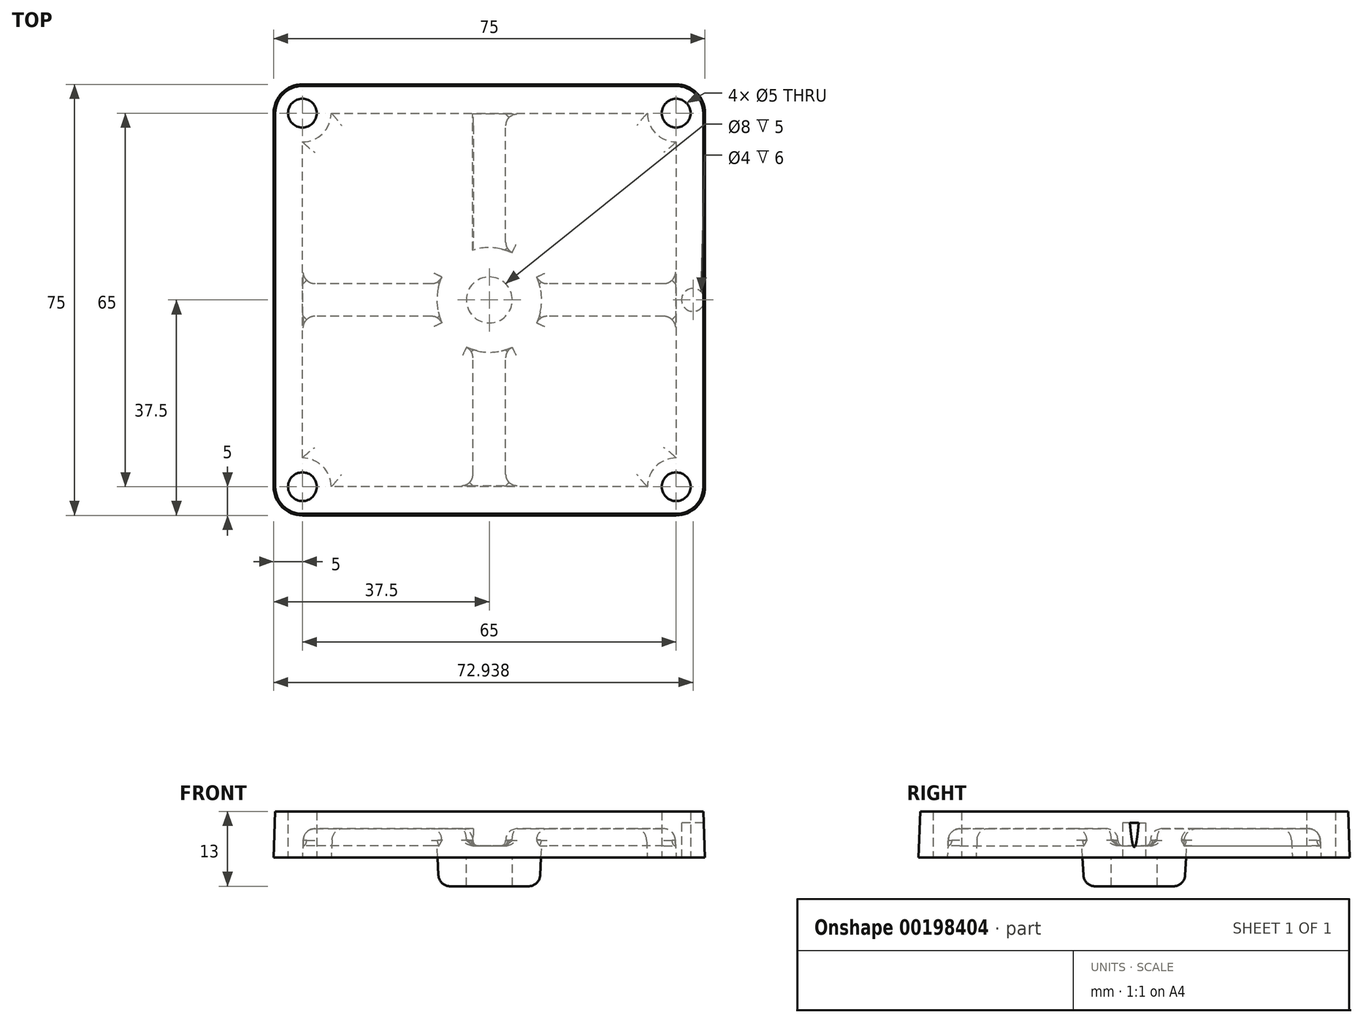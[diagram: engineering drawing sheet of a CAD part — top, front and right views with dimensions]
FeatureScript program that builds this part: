
annotation { "Feature Type Name" : "Feature", "Feature Type Description" : "" }
export const myFeature = defineFeature(function(context is Context, id is Id, definition is map)
    precondition{}
    {
        {
            var Q0;
            Q0=qCreatedBy(makeId("Top.planeOp"),FACE);
            var sketch = newSketch(context, id + "F0", { "sketchPlane" : qUnion([Q0])});
            skLineSegment(sketch, "E0.bottom", {"start": v(-32.5, -37.5) * mm, "end": v(32.5, -37.5) * mm});
            skLineSegment(sketch, "E0.top", {"start": v(-32.5, 37.5) * mm, "end": v(32.5, 37.5) * mm});
            skLineSegment(sketch, "E0.left", {"start": v(-37.5, -32.5) * mm, "end": v(-37.5, 32.5) * mm});
            skLineSegment(sketch, "E0.right", {"start": v(37.5, -32.5) * mm, "end": v(37.5, 32.5) * mm});
            skPoint(sketch, "E0.middle", {"position": v(0, 0) * mm});
            skPoint(sketch, "E1.visualSharp", {"position": v(-37.5, 37.5) * mm});
            skArc(sketch, "E1.filletArc", {"start": v(-32.5, 37.5) * mm, "mid": v(-36.04, 36.04) * mm, "end": v(-37.5, 32.5) * mm});
            skPoint(sketch, "E2.visualSharp", {"position": v(37.5, 37.5) * mm});
            skArc(sketch, "E2.filletArc", {"start": v(37.5, 32.5) * mm, "mid": v(36.04, 36.04) * mm, "end": v(32.5, 37.5) * mm});
            skPoint(sketch, "E3.visualSharp", {"position": v(37.5, -37.5) * mm});
            skArc(sketch, "E3.filletArc", {"start": v(32.5, -37.5) * mm, "mid": v(36.04, -36.04) * mm, "end": v(37.5, -32.5) * mm});
            skPoint(sketch, "E4.visualSharp", {"position": v(-37.5, -37.5) * mm});
            skArc(sketch, "E4.filletArc", {"start": v(-37.5, -32.5) * mm, "mid": v(-36.04, -36.04) * mm, "end": v(-32.5, -37.5) * mm});
            skSolve(sketch);
        }
        {
            var Q0;
            Q0=makeQuery(id+"F0.imprint","IMPRINT",FACE,{"disambiguationData":[TD([[makeQuery(id+"F0.imprint","IMPRINT",EDGE,{"derivedFrom":sQuery(id+"F0.wireOp",EDGE,"E0.bottom")}),1.0]])]});
            extrude(context, id + "F1", {"entities" : qUnion([Q0]), "depth" : 8 * mm, "hasDraft" : true, "draftAngle" : 2 * degree, "draftPullDirection" : true, "offsetDistance" : 25 * mm});
        }
        {
            var Q0;
            Q0=qCreatedBy(makeId("Top.planeOp"),FACE);
            var sketch = newSketch(context, id + "F2", { "sketchPlane" : qUnion([Q0])});
            skCircle(sketch, "E5", {"center": v(0, 0) * mm, "radius": 9 * mm});
            skLineSegment(sketch, "E6.bottom", {"start": v(-27.5, -32.5) * mm, "end": v(27.5, -32.5) * mm});
            skLineSegment(sketch, "E6.top", {"start": v(-27.5, 32.5) * mm, "end": v(27.5, 32.5) * mm});
            skLineSegment(sketch, "E6.left", {"start": v(-32.5, -27.5) * mm, "end": v(-32.5, 27.5) * mm});
            skLineSegment(sketch, "E6.right", {"start": v(32.5, -27.5) * mm, "end": v(32.5, 27.5) * mm});
            skArc(sketch, "E7", {"start": v(-27.5, 32.5) * mm, "mid": v(-28.96, 28.96) * mm, "end": v(-32.5, 27.5) * mm});
            skArc(sketch, "E8", {"start": v(-32.5, -27.5) * mm, "mid": v(-28.96, -28.96) * mm, "end": v(-27.5, -32.5) * mm});
            skArc(sketch, "E9", {"start": v(27.5, -32.5) * mm, "mid": v(28.96, -28.96) * mm, "end": v(32.5, -27.5) * mm});
            skArc(sketch, "E10", {"start": v(27.5, 32.5) * mm, "mid": v(28.96, 28.96) * mm, "end": v(32.5, 27.5) * mm});
            skSolve(sketch);
        }
        {
            var Q0;
            Q0=makeQuery(id+"F2.imprint","IMPRINT",FACE,{"disambiguationData":[TD([[makeQuery(id+"F2.imprint","IMPRINT",EDGE,{"derivedFrom":sQuery(id+"F2.wireOp",EDGE,"E5")}),-1.0]])]});
            extrude(context, id + "F3", {"entities" : qUnion([Q0]), "operationType" : NewBodyOperationType.REMOVE, "depth" : 5 * mm, "hasDraft" : true, "draftAngle" : 3 * degree, "draftPullDirection" : true, "offsetDistance" : 25 * mm});
        }
        {
            var Q0;
            Q0=makeQuery(id+"F3.boolean.opBoolean","COPY",EDGE,{"derivedFrom":makeQuery(id+"F3.opExtrude","CAP_EDGE",EDGE,{"disambiguationData":[OSD([sQuery(id+"F2.wireOp",EDGE,"E6.top")])],"isStart":false})});
            var Q1;
            Q1=makeQuery(id+"F3.boolean.opBoolean","COPY",EDGE,{"derivedFrom":makeQuery(id+"F3.opExtrude","CAP_EDGE",EDGE,{"disambiguationData":[OSD([sQuery(id+"F2.wireOp",EDGE,"E7")])],"isStart":false})});
            var Q2;
            Q2=makeQuery(id+"F3.boolean.opBoolean","COPY",EDGE,{"derivedFrom":makeQuery(id+"F3.opExtrude","CAP_EDGE",EDGE,{"disambiguationData":[OSD([sQuery(id+"F2.wireOp",EDGE,"E10")])],"isStart":false})});
            var Q3;
            Q3=makeQuery(id+"F3.boolean.opBoolean","COPY",EDGE,{"derivedFrom":makeQuery(id+"F3.opExtrude","CAP_EDGE",EDGE,{"disambiguationData":[OSD([sQuery(id+"F2.wireOp",EDGE,"E6.right")])],"isStart":false})});
            var Q4;
            Q4=makeQuery(id+"F3.boolean.opBoolean","COPY",EDGE,{"derivedFrom":makeQuery(id+"F3.opExtrude","CAP_EDGE",EDGE,{"disambiguationData":[OSD([sQuery(id+"F2.wireOp",EDGE,"E9")])],"isStart":false})});
            var Q5;
            Q5=makeQuery(id+"F3.boolean.opBoolean","COPY",EDGE,{"derivedFrom":makeQuery(id+"F3.opExtrude","CAP_EDGE",EDGE,{"disambiguationData":[OSD([sQuery(id+"F2.wireOp",EDGE,"E8")])],"isStart":false})});
            var Q6;
            Q6=makeQuery(id+"F3.boolean.opBoolean","COPY",EDGE,{"derivedFrom":makeQuery(id+"F3.opExtrude","CAP_EDGE",EDGE,{"disambiguationData":[OSD([sQuery(id+"F2.wireOp",EDGE,"E6.bottom")])],"isStart":false})});
            var Q7;
            Q7=makeQuery(id+"F3.boolean.opBoolean","COPY",EDGE,{"derivedFrom":makeQuery(id+"F3.opExtrude","CAP_EDGE",EDGE,{"disambiguationData":[OSD([sQuery(id+"F2.wireOp",EDGE,"E6.left")])],"isStart":false})});
            fillet(context, id + "F4", {"entities" : qUnion([Q0, Q1, Q2, Q3, Q4, Q5, Q6, Q7]), "radius" : 2 * mm, "tangentPropagation" : true, "allowEdgeOverflow" : false});
        }
        {
            var Q0;
            Q0=qCreatedBy(makeId("Top.planeOp"),FACE);
            var sketch = newSketch(context, id + "F5", { "sketchPlane" : qUnion([Q0])});
            skPoint(sketch, "E11.middle", {"position": v(0, 0) * mm});
            skCircle(sketch, "E12", {"center": v(-32.5, 32.5) * mm, "radius": 2.5 * mm});
            skPoint(sketch, "E11.right.start.orphan", {"position": v(32.5, 32.5) * mm});
            skPoint(sketch, "E11.top.end.orphan", {"position": v(32.5, -32.5) * mm});
            skPoint(sketch, "E11.top.start.orphan", {"position": v(-32.5, -32.5) * mm});
            skCircle(sketch, "E13", {"center": v(-32.5, -32.5) * mm, "radius": 2.5 * mm});
            skCircle(sketch, "E14", {"center": v(32.5, -32.5) * mm, "radius": 2.5 * mm});
            skCircle(sketch, "E15", {"center": v(32.5, 32.5) * mm, "radius": 2.5 * mm});
            skSolve(sketch);
        }
        {
            var Q0;
            Q0=makeQuery(id+"F5.imprint","IMPRINT",FACE,{"disambiguationData":[TD([[makeQuery(id+"F5.imprint","IMPRINT",EDGE,{"derivedFrom":sQuery(id+"F5.wireOp",EDGE,"E13")}),1.0]])]});
            var Q1;
            Q1=makeQuery(id+"F5.imprint","IMPRINT",FACE,{"disambiguationData":[TD([[makeQuery(id+"F5.imprint","IMPRINT",EDGE,{"derivedFrom":sQuery(id+"F5.wireOp",EDGE,"E12")}),1.0]])]});
            var Q2;
            Q2=makeQuery(id+"F5.imprint","IMPRINT",FACE,{"disambiguationData":[TD([[makeQuery(id+"F5.imprint","IMPRINT",EDGE,{"derivedFrom":sQuery(id+"F5.wireOp",EDGE,"E15")}),1.0]])]});
            var Q3;
            Q3=makeQuery(id+"F5.imprint","IMPRINT",FACE,{"disambiguationData":[TD([[makeQuery(id+"F5.imprint","IMPRINT",EDGE,{"derivedFrom":sQuery(id+"F5.wireOp",EDGE,"E14")}),1.0]])]});
            extrude(context, id + "F6", {"entities" : qUnion([Q0, Q1, Q2, Q3]), "operationType" : NewBodyOperationType.REMOVE, "depth" : 25 * mm, "hasSecondDirection" : true, "secondDirectionOppositeDirection" : true, "secondDirectionDepth" : 25 * mm});
        }
        {
            var Q0;
            Q0=makeQuery(id+"F3.boolean.opBoolean","COPY",EDGE,{"derivedFrom":makeQuery(id+"F3.opExtrude","CAP_EDGE",EDGE,{"disambiguationData":[OSD([sQuery(id+"F2.wireOp",EDGE,"E5")])],"isStart":false})});
            fillet(context, id + "F7", {"entities" : qUnion([Q0]), "radius" : 2 * mm, "tangentPropagation" : true, "allowEdgeOverflow" : false});
        }
        {
            var Q0;
            Q0=qCreatedBy(makeId("Top.planeOp"),FACE);
            var sketch = newSketch(context, id + "F8", { "sketchPlane" : qUnion([Q0])});
            skLineSegment(sketch, "E16.bottom", {"start": v(-35, -3) * mm, "end": v(-3, -3) * mm});
            skLineSegment(sketch, "E16.top", {"start": v(-35, 3) * mm, "end": v(-3, 3) * mm});
            skLineSegment(sketch, "E16.left", {"start": v(-35, -3) * mm, "end": v(-35, 3) * mm});
            skLineSegment(sketch, "E16.right", {"start": v(35, -3) * mm, "end": v(35, 3) * mm});
            skPoint(sketch, "E16.middle", {"position": v(0, 0) * mm});
            skLineSegment(sketch, "E17.bottom", {"start": v(3, 35) * mm, "end": v(-3, 35) * mm});
            skLineSegment(sketch, "E17.top", {"start": v(3, -35) * mm, "end": v(-3, -35) * mm});
            skLineSegment(sketch, "E17.left", {"start": v(3, 35) * mm, "end": v(3, 3) * mm});
            skLineSegment(sketch, "E17.right", {"start": v(-3, 35) * mm, "end": v(-3, 3) * mm});
            skLineSegment(sketch, "E18.trimOffspring", {"start": v(-3, -3) * mm, "end": v(-3, -35) * mm});
            skLineSegment(sketch, "E19.trimOffspring", {"start": v(3, -3) * mm, "end": v(35, -3) * mm});
            skLineSegment(sketch, "E20.trimOffspring", {"start": v(3, -3) * mm, "end": v(3, -35) * mm});
            skLineSegment(sketch, "E21.trimOffspring", {"start": v(3, 3) * mm, "end": v(35, 3) * mm});
            skSolve(sketch);
        }
        {
            var Q0;
            Q0 = qSketchRegion(id + "F8", true);
            extrude(context, id + "F9", {"entities" : qUnion([Q0]), "operationType" : NewBodyOperationType.ADD, "depth" : 7 * mm, "hasDraft" : true, "draftAngle" : 3 * degree, "draftPullDirection" : true, "hasSecondDirection" : true, "secondDirectionOppositeDirection" : false, "secondDirectionDepth" : 2 * mm, "offsetDistance" : 25 * mm});
        }
        {
            var Q0;
            Q0=makeQuery(id+"F9.boolean.opBoolean","INTERSECT",EDGE,{"derivedFrom":[makeQuery(id+"F3.boolean.opBoolean","COPY",FACE,{"derivedFrom":makeQuery(id+"F3.opExtrude","CAP_FACE",FACE,{"disambiguationData":[OSD([sQuery(id+"F2.wireOp",EDGE,"E5"),sQuery(id+"F2.wireOp",EDGE,"E6.bottom"),sQuery(id+"F2.wireOp",EDGE,"E6.top"),sQuery(id+"F2.wireOp",EDGE,"E6.left"),sQuery(id+"F2.wireOp",EDGE,"E6.right"),sQuery(id+"F2.wireOp",EDGE,"E7"),sQuery(id+"F2.wireOp",EDGE,"E8"),sQuery(id+"F2.wireOp",EDGE,"E9"),sQuery(id+"F2.wireOp",EDGE,"E10")])],"isStart":false})}),makeQuery(id+"F9.opExtrude","SWEPT_FACE",FACE,{"disambiguationData":[OSD([sQuery(id+"F8.wireOp",EDGE,"E18.trimOffspring")])]})]});
            var Q1;
            Q1=makeQuery(id+"F9.boolean.opBoolean","INTERSECT",EDGE,{"derivedFrom":[makeQuery(id+"F3.boolean.opBoolean","COPY",FACE,{"derivedFrom":makeQuery(id+"F3.opExtrude","CAP_FACE",FACE,{"disambiguationData":[OSD([sQuery(id+"F2.wireOp",EDGE,"E5"),sQuery(id+"F2.wireOp",EDGE,"E6.bottom"),sQuery(id+"F2.wireOp",EDGE,"E6.top"),sQuery(id+"F2.wireOp",EDGE,"E6.left"),sQuery(id+"F2.wireOp",EDGE,"E6.right"),sQuery(id+"F2.wireOp",EDGE,"E7"),sQuery(id+"F2.wireOp",EDGE,"E8"),sQuery(id+"F2.wireOp",EDGE,"E9"),sQuery(id+"F2.wireOp",EDGE,"E10")])],"isStart":false})}),makeQuery(id+"F9.opExtrude","SWEPT_FACE",FACE,{"disambiguationData":[OSD([sQuery(id+"F8.wireOp",EDGE,"E16.bottom")])]})]});
            var Q2;
            Q2=makeQuery(id+"F9.boolean.opBoolean","INTERSECT",EDGE,{"derivedFrom":[makeQuery(id+"F3.boolean.opBoolean","COPY",FACE,{"derivedFrom":makeQuery(id+"F3.opExtrude","CAP_FACE",FACE,{"disambiguationData":[OSD([sQuery(id+"F2.wireOp",EDGE,"E5"),sQuery(id+"F2.wireOp",EDGE,"E6.bottom"),sQuery(id+"F2.wireOp",EDGE,"E6.top"),sQuery(id+"F2.wireOp",EDGE,"E6.left"),sQuery(id+"F2.wireOp",EDGE,"E6.right"),sQuery(id+"F2.wireOp",EDGE,"E7"),sQuery(id+"F2.wireOp",EDGE,"E8"),sQuery(id+"F2.wireOp",EDGE,"E9"),sQuery(id+"F2.wireOp",EDGE,"E10")])],"isStart":false})}),makeQuery(id+"F9.opExtrude","SWEPT_FACE",FACE,{"disambiguationData":[OSD([sQuery(id+"F8.wireOp",EDGE,"E19.trimOffspring")])]})]});
            var Q3;
            Q3=makeQuery(id+"F9.boolean.opBoolean","INTERSECT",EDGE,{"derivedFrom":[makeQuery(id+"F3.boolean.opBoolean","COPY",FACE,{"derivedFrom":makeQuery(id+"F3.opExtrude","CAP_FACE",FACE,{"disambiguationData":[OSD([sQuery(id+"F2.wireOp",EDGE,"E5"),sQuery(id+"F2.wireOp",EDGE,"E6.bottom"),sQuery(id+"F2.wireOp",EDGE,"E6.top"),sQuery(id+"F2.wireOp",EDGE,"E6.left"),sQuery(id+"F2.wireOp",EDGE,"E6.right"),sQuery(id+"F2.wireOp",EDGE,"E7"),sQuery(id+"F2.wireOp",EDGE,"E8"),sQuery(id+"F2.wireOp",EDGE,"E9"),sQuery(id+"F2.wireOp",EDGE,"E10")])],"isStart":false})}),makeQuery(id+"F9.opExtrude","SWEPT_FACE",FACE,{"disambiguationData":[OSD([sQuery(id+"F8.wireOp",EDGE,"E21.trimOffspring")])]})]});
            var Q4;
            Q4=makeQuery(id+"F9.boolean.opBoolean","INTERSECT",EDGE,{"derivedFrom":[makeQuery(id+"F3.boolean.opBoolean","COPY",FACE,{"derivedFrom":makeQuery(id+"F3.opExtrude","CAP_FACE",FACE,{"disambiguationData":[OSD([sQuery(id+"F2.wireOp",EDGE,"E5"),sQuery(id+"F2.wireOp",EDGE,"E6.bottom"),sQuery(id+"F2.wireOp",EDGE,"E6.top"),sQuery(id+"F2.wireOp",EDGE,"E6.left"),sQuery(id+"F2.wireOp",EDGE,"E6.right"),sQuery(id+"F2.wireOp",EDGE,"E7"),sQuery(id+"F2.wireOp",EDGE,"E8"),sQuery(id+"F2.wireOp",EDGE,"E9"),sQuery(id+"F2.wireOp",EDGE,"E10")])],"isStart":false})}),makeQuery(id+"F9.opExtrude","SWEPT_FACE",FACE,{"disambiguationData":[OSD([sQuery(id+"F8.wireOp",EDGE,"E16.top")])]})]});
            var Q5;
            Q5=makeQuery(id+"F9.boolean.opBoolean","INTERSECT",EDGE,{"derivedFrom":[makeQuery(id+"F3.boolean.opBoolean","COPY",FACE,{"derivedFrom":makeQuery(id+"F3.opExtrude","CAP_FACE",FACE,{"disambiguationData":[OSD([sQuery(id+"F2.wireOp",EDGE,"E5"),sQuery(id+"F2.wireOp",EDGE,"E6.bottom"),sQuery(id+"F2.wireOp",EDGE,"E6.top"),sQuery(id+"F2.wireOp",EDGE,"E6.left"),sQuery(id+"F2.wireOp",EDGE,"E6.right"),sQuery(id+"F2.wireOp",EDGE,"E7"),sQuery(id+"F2.wireOp",EDGE,"E8"),sQuery(id+"F2.wireOp",EDGE,"E9"),sQuery(id+"F2.wireOp",EDGE,"E10")])],"isStart":false})}),makeQuery(id+"F9.opExtrude","SWEPT_FACE",FACE,{"disambiguationData":[OSD([sQuery(id+"F8.wireOp",EDGE,"E20.trimOffspring")])]})]});
            var Q6;
            Q6=makeQuery(id+"F9.boolean.opBoolean","INTERSECT",EDGE,{"derivedFrom":[makeQuery(id+"F3.boolean.opBoolean","COPY",FACE,{"derivedFrom":makeQuery(id+"F3.opExtrude","CAP_FACE",FACE,{"disambiguationData":[OSD([sQuery(id+"F2.wireOp",EDGE,"E5"),sQuery(id+"F2.wireOp",EDGE,"E6.bottom"),sQuery(id+"F2.wireOp",EDGE,"E6.top"),sQuery(id+"F2.wireOp",EDGE,"E6.left"),sQuery(id+"F2.wireOp",EDGE,"E6.right"),sQuery(id+"F2.wireOp",EDGE,"E7"),sQuery(id+"F2.wireOp",EDGE,"E8"),sQuery(id+"F2.wireOp",EDGE,"E9"),sQuery(id+"F2.wireOp",EDGE,"E10")])],"isStart":false})}),makeQuery(id+"F9.opExtrude","SWEPT_FACE",FACE,{"disambiguationData":[OSD([sQuery(id+"F8.wireOp",EDGE,"E17.left")])]})]});
            fillet(context, id + "F10", {"entities" : qUnion([Q0, Q1, Q2, Q3, Q4, Q5, Q6]), "radius" : 2 * mm, "tangentPropagation" : true, "allowEdgeOverflow" : false});
        }
        {
            var Q0;
            Q0=makeQuery(id+"F9.opExtrude","CAP_EDGE",EDGE,{"disambiguationData":[OSD([sQuery(id+"F8.wireOp",EDGE,"E17.left")])],"isStart":true});
            var Q1;
            Q1=makeQuery(id+"F9.opExtrude","CAP_EDGE",EDGE,{"disambiguationData":[OSD([sQuery(id+"F8.wireOp",EDGE,"E16.top")])],"isStart":true});
            var Q2;
            Q2=makeQuery(id+"F9.opExtrude","CAP_EDGE",EDGE,{"disambiguationData":[OSD([sQuery(id+"F8.wireOp",EDGE,"E18.trimOffspring")])],"isStart":true});
            var Q3;
            Q3=makeQuery(id+"F9.opExtrude","CAP_EDGE",EDGE,{"disambiguationData":[OSD([sQuery(id+"F8.wireOp",EDGE,"E20.trimOffspring")])],"isStart":true});
            var Q4;
            Q4=makeQuery(id+"F9.opExtrude","CAP_EDGE",EDGE,{"disambiguationData":[OSD([sQuery(id+"F8.wireOp",EDGE,"E16.bottom")])],"isStart":true});
            var Q5;
            Q5=makeQuery(id+"F9.opExtrude","CAP_EDGE",EDGE,{"disambiguationData":[OSD([sQuery(id+"F8.wireOp",EDGE,"E19.trimOffspring")])],"isStart":true});
            var Q6;
            Q6=makeQuery(id+"F9.opExtrude","CAP_EDGE",EDGE,{"disambiguationData":[OSD([sQuery(id+"F8.wireOp",EDGE,"E21.trimOffspring")])],"isStart":true});
            var Q7;
            Q7=makeQuery(id+"F3.boolean.opBoolean","COPY",EDGE,{"derivedFrom":makeQuery(id+"F3.opExtrude","CAP_EDGE",EDGE,{"disambiguationData":[OSD([sQuery(id+"F2.wireOp",EDGE,"E6.right")])],"isStart":true})});
            var Q8;
            Q8=makeQuery(id+"F3.boolean.opBoolean","COPY",EDGE,{"derivedFrom":makeQuery(id+"F3.opExtrude","CAP_EDGE",EDGE,{"disambiguationData":[OSD([sQuery(id+"F2.wireOp",EDGE,"E10")])],"isStart":true})});
            var Q9;
            Q9=makeQuery(id+"F3.boolean.opBoolean","COPY",EDGE,{"derivedFrom":makeQuery(id+"F3.opExtrude","CAP_EDGE",EDGE,{"disambiguationData":[OSD([sQuery(id+"F2.wireOp",EDGE,"E6.top")])],"isStart":true})});
            var Q10;
            Q10=makeQuery(id+"F3.boolean.opBoolean","COPY",EDGE,{"derivedFrom":makeQuery(id+"F3.opExtrude","CAP_EDGE",EDGE,{"disambiguationData":[OSD([sQuery(id+"F2.wireOp",EDGE,"E7")])],"isStart":true})});
            var Q11;
            Q11=makeQuery(id+"F3.boolean.opBoolean","COPY",EDGE,{"derivedFrom":makeQuery(id+"F3.opExtrude","CAP_EDGE",EDGE,{"disambiguationData":[OSD([sQuery(id+"F2.wireOp",EDGE,"E6.left")])],"isStart":true})});
            var Q12;
            Q12=makeQuery(id+"F3.boolean.opBoolean","COPY",EDGE,{"derivedFrom":makeQuery(id+"F3.opExtrude","CAP_EDGE",EDGE,{"disambiguationData":[OSD([sQuery(id+"F2.wireOp",EDGE,"E8")])],"isStart":true})});
            var Q13;
            Q13=makeQuery(id+"F3.boolean.opBoolean","COPY",EDGE,{"derivedFrom":makeQuery(id+"F3.opExtrude","CAP_EDGE",EDGE,{"disambiguationData":[OSD([sQuery(id+"F2.wireOp",EDGE,"E6.bottom")])],"isStart":true})});
            var Q14;
            Q14=makeQuery(id+"F3.boolean.opBoolean","COPY",EDGE,{"derivedFrom":makeQuery(id+"F3.opExtrude","CAP_EDGE",EDGE,{"disambiguationData":[OSD([sQuery(id+"F2.wireOp",EDGE,"E9")])],"isStart":true})});
            fillet(context, id + "F11", {"entities" : qUnion([Q0, Q1, Q2, Q3, Q4, Q5, Q6, Q7, Q8, Q9, Q10, Q11, Q12, Q13, Q14]), "radius" : 1 * mm, "tangentPropagation" : true, "allowEdgeOverflow" : false});
        }
        {
            var Q0;
            Q0=qCreatedBy(makeId("Top.planeOp"),FACE);
            var sketch = newSketch(context, id + "F12", { "sketchPlane" : qUnion([Q0])});
            skCircle(sketch, "E22", {"center": v(0, 0) * mm, "radius": 9 * mm});
            skSolve(sketch);
        }
        {
            var Q0;
            Q0 = qSketchRegion(id + "F12", true);
            extrude(context, id + "F13", {"entities" : qUnion([Q0]), "operationType" : NewBodyOperationType.ADD, "oppositeDirection" : true, "depth" : 5 * mm, "hasDraft" : true, "draftAngle" : 3 * degree, "draftPullDirection" : true});
        }
        {
            var Q0;
            Q0=makeQuery(id+"F13.opExtrude","CAP_EDGE",EDGE,{"disambiguationData":[OSD([sQuery(id+"F12.wireOp",EDGE,"E22")])],"isStart":false});
            fillet(context, id + "F14", {"entities" : qUnion([Q0]), "radius" : 2 * mm, "tangentPropagation" : true, "allowEdgeOverflow" : false});
        }
        {
            var Q0;
            Q0=qCreatedBy(makeId("Top.planeOp"),FACE);
            var sketch = newSketch(context, id + "F15", { "sketchPlane" : qUnion([Q0])});
            skCircle(sketch, "E23", {"center": v(0, 0) * mm, "radius": 4 * mm});
            skSolve(sketch);
        }
        {
            var Q0;
            Q0 = qSketchRegion(id + "F15", true);
            extrude(context, id + "F16", {"entities" : qUnion([Q0]), "operationType" : NewBodyOperationType.REMOVE, "oppositeDirection" : true, "depth" : 25 * mm});
        }
        {
            var Q0;
            Q0=qCreatedBy(makeId("Top.planeOp"),FACE);
            var sketch = newSketch(context, id + "F17", { "sketchPlane" : qUnion([Q0])});
            skCircle(sketch, "E24", {"center": v(35.44, 0) * mm, "radius": 2 * mm});
            skSolve(sketch);
        }
        {
            var Q0;
            Q0=makeQuery(id+"F17.imprint","IMPRINT",FACE,{"disambiguationData":[TD([[makeQuery(id+"F17.imprint","IMPRINT",EDGE,{"derivedFrom":sQuery(id+"F17.wireOp",EDGE,"E24")}),1.0]])]});
            extrude(context, id + "F18", {"entities" : qUnion([Q0]), "operationType" : NewBodyOperationType.REMOVE, "depth" : 6 * mm});
        }
    });
